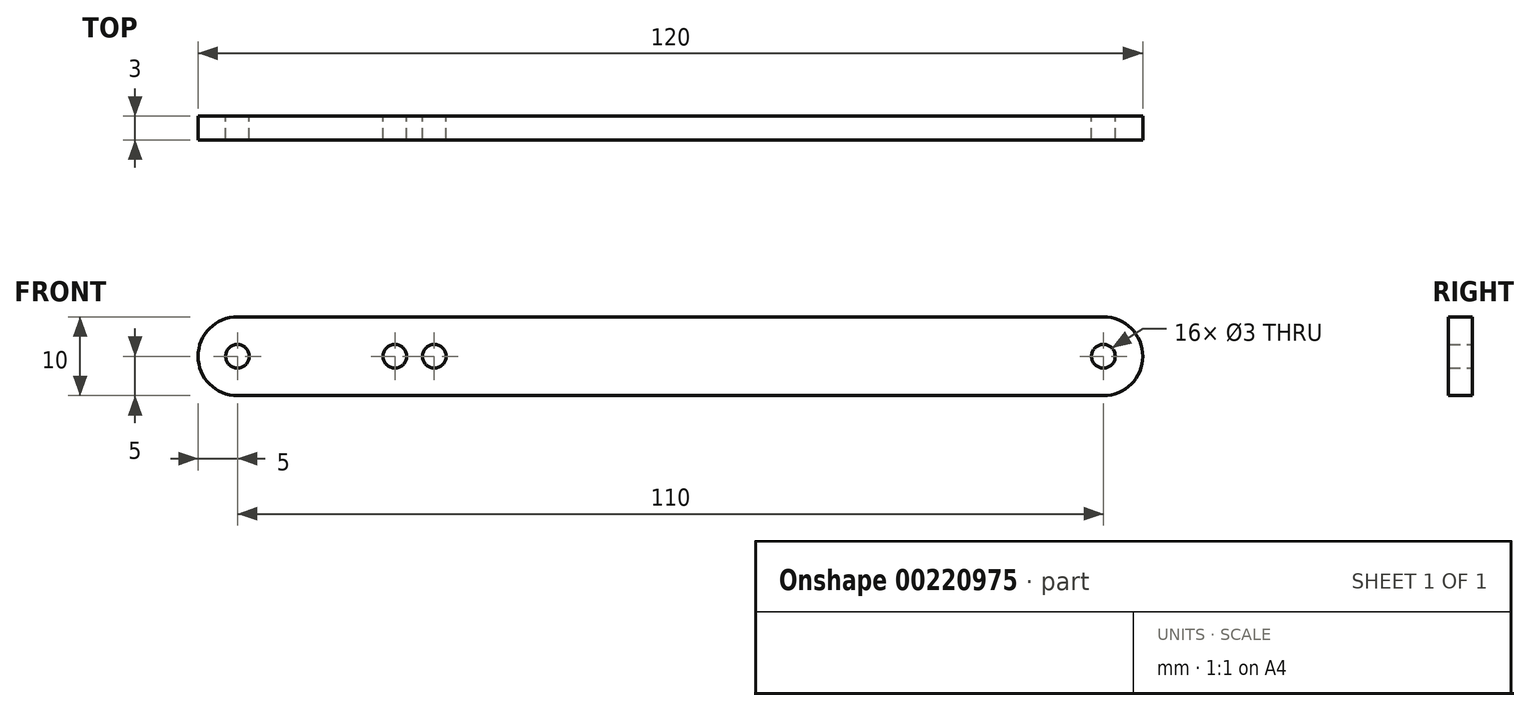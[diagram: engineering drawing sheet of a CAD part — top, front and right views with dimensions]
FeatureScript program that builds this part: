
annotation { "Feature Type Name" : "Feature", "Feature Type Description" : "" }
export const myFeature = defineFeature(function(context is Context, id is Id, definition is map)
    precondition{}
    {
        {
            var Q0;
            Q0=qCreatedBy(makeId("Front.planeOp"),FACE);
            var sketch = newSketch(context, id + "F0", { "sketchPlane" : qUnion([Q0])});
            skCircle(sketch, "E0", {"center": v(-25, 0) * mm, "radius": 1.5 * mm});
            skArc(sketch, "E1", {"start": v(-25, 5) * mm, "mid": v(-30, 0) * mm, "end": v(-25, -5) * mm});
            skCircle(sketch, "E2", {"center": v(85, 0) * mm, "radius": 1.5 * mm});
            skLineSegment(sketch, "E3", {"start": v(-25, 5) * mm, "end": v(85, 5) * mm});
            skLineSegment(sketch, "E4", {"start": v(-25, -5) * mm, "end": v(85, -5) * mm});
            skArc(sketch, "E5", {"start": v(85, 5) * mm, "mid": v(90, 0) * mm, "end": v(85, -5) * mm});
            skCircle(sketch, "E6", {"center": v(-5, 0) * mm, "radius": 1.5 * mm});
            skCircle(sketch, "E7", {"center": v(0, 0) * mm, "radius": 1.5 * mm});
            skSolve(sketch);
        }
        {
            var Q0;
            Q0=makeQuery(id+"F0.imprint","IMPRINT",FACE,{"disambiguationData":[TD([[makeQuery(id+"F0.imprint","IMPRINT",EDGE,{"derivedFrom":sQuery(id+"F0.wireOp",EDGE,"E0")}),-1.0]])]});
            extrude(context, id + "F1", {"entities" : qUnion([Q0]), "depth" : 3 * mm});
        }
    });
